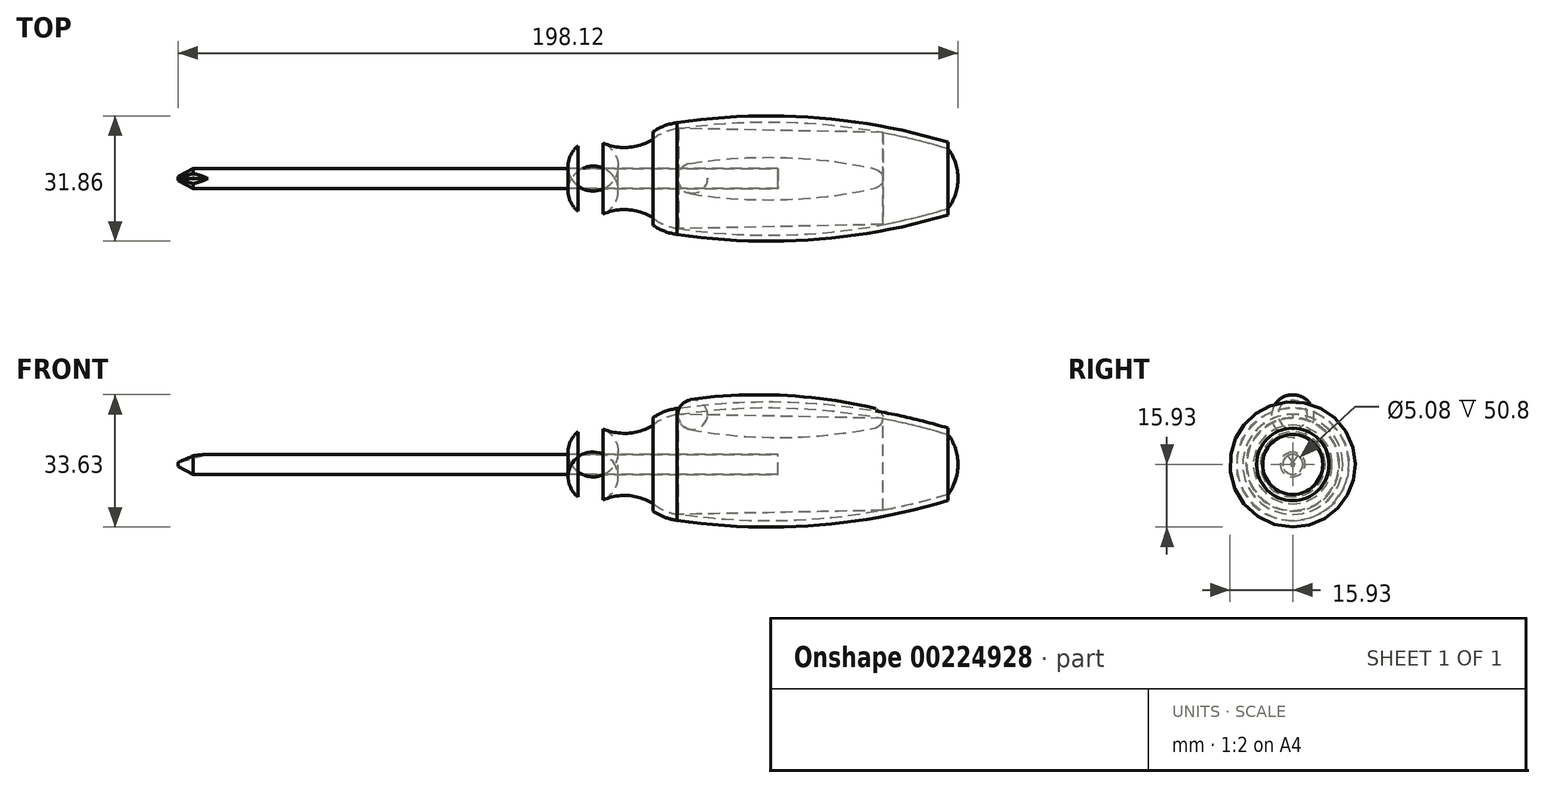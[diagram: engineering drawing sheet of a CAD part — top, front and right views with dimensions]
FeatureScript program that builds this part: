
annotation { "Feature Type Name" : "Feature", "Feature Type Description" : "" }
export const myFeature = defineFeature(function(context is Context, id is Id, definition is map)
    precondition{}
    {
        {
            var Q0;
            Q0=qCreatedBy(makeId("Front.planeOp"),FACE);
            var sketch = newSketch(context, id + "F0", { "sketchPlane" : qUnion([Q0])});
            skLineSegment(sketch, "E0", {"start": v(-101.6, 0) * mm, "end": v(0, 0) * mm});
            skLineSegment(sketch, "E1", {"start": v(0, 0) * mm, "end": v(96.52, 0) * mm});
            skLineSegment(sketch, "E2", {"start": v(0, 8.26) * mm, "end": v(0, 2.54) * mm});
            skLineSegment(sketch, "E3", {"start": v(0, 2.54) * mm, "end": v(-97.8, 2.54) * mm});
            skLineSegment(sketch, "E4", {"start": v(-97.8, 2.54) * mm, "end": v(-101.6, 0.5) * mm});
            skLineSegment(sketch, "E5", {"start": v(-101.6, 0.5) * mm, "end": v(-101.6, 0) * mm});
            skArc(sketch, "E6", {"start": v(6.35, 9.01) * mm, "mid": v(3.07, 9.5) * mm, "end": v(0, 8.26) * mm});
            skArc(sketch, "E7", {"start": v(6.35, 9.01) * mm, "mid": v(12.82, 7.93) * mm, "end": v(19.05, 10) * mm});
            skArc(sketch, "E8", {"start": v(25.4, 12.7) * mm, "mid": v(22.04, 11.78) * mm, "end": v(19.05, 10) * mm});
            skArc(sketch, "E9", {"start": v(96.52, 0) * mm, "mid": v(95.87, 4.02) * mm, "end": v(93.98, 7.62) * mm});
            skArc(sketch, "E10", {"start": v(93.98, 7.62) * mm, "mid": v(59.97, 13.98) * mm, "end": v(25.4, 12.7) * mm});
            skArc(sketch, "E11.0", {"start": v(25.2, 14.21) * mm, "mid": v(22, 13.4) * mm, "end": v(19.05, 11.88) * mm});
            skArc(sketch, "E12.0", {"start": v(93.98, 9.21) * mm, "mid": v(59.85, 15.52) * mm, "end": v(25.17, 14.2) * mm});
            skLineSegment(sketch, "E13", {"start": v(19.05, 10) * mm, "end": v(19.05, 11.88) * mm});
            skLineSegment(sketch, "E14", {"start": v(93.98, 9.21) * mm, "end": v(93.98, 7.62) * mm});
            skLineSegment(sketch, "E15", {"start": v(0, 2.54) * mm, "end": v(50.8, 2.54) * mm});
            skLineSegment(sketch, "E16", {"start": v(50.8, 2.54) * mm, "end": v(50.8, 0) * mm});
            skPoint(sketch, "E17", {"position": v(77.47, 11.69) * mm});
            skLineSegment(sketch, "E18", {"start": v(0, 0) * mm, "end": v(115.04, 0) * mm, "construction": true});
            skSolve(sketch);
        }
        {
            var Q0;
            Q0=makeQuery(id+"F0.imprint","IMPRINT",FACE,{"disambiguationData":[TD([[makeQuery(id+"F0.imprint","IMPRINT",EDGE,{"derivedFrom":sQuery(id+"F0.wireOp",EDGE,"E2")}),1.0]])]});
            var sketch = newSketch(context, id + "F1", { "sketchPlane" : qUnion([Q0])});
            skLineSegment(sketch, "E19", {"start": v(25.3, 12.73) * mm, "end": v(77.46, 11.69) * mm});
            skArc(sketch, "E20", {"start": v(28.6, 16.51) * mm, "mid": v(26.24, 15.24) * mm, "end": v(25.3, 12.73) * mm});
            skArc(sketch, "E21", {"start": v(77.46, 11.69) * mm, "mid": v(76.93, 13.28) * mm, "end": v(75.51, 14.2) * mm});
            skArc(sketch, "E22", {"start": v(75.51, 14.2) * mm, "mid": v(52.16, 17.54) * mm, "end": v(28.6, 16.51) * mm});
            skLineSegment(sketch, "E23", {"start": v(25.3, 12.73) * mm, "end": v(77.46, 11.69) * mm, "construction": true});
            skSolve(sketch);
        }
        {
            var Q0;
            {var subQ1=sQuery(id+"F0.wireOp",EDGE,"E0");Q0=makeQuery(id+"F0.imprint","IMPRINT",FACE,{"disambiguationData":[TD([[makeQuery(id+"F0.imprint","IMPRINT",EDGE,{"derivedFrom":subQ1}),1.0]])]});}
            var Q1;
            Q1=sQuery(id+"F0.wireOp",EDGE,"E18");
            revolve(context, id + "F2", {"entities" : qUnion([Q0]), "axis" : qUnion([Q1]), "revolveType" : RevolveType.FULL});
        }
        {
            var Q0;
            Q0=makeQuery(id+"F1.imprint","IMPRINT",FACE,{"disambiguationData":[TD([[makeQuery(id+"F1.imprint","IMPRINT",EDGE,{"derivedFrom":makeQuery(id+"F0.imprint","IMPRINT",EDGE,{"derivedFrom":sQuery(id+"F0.wireOp",EDGE,"E2")})}),1.0]])]});
            var Q1;
            Q1=makeQuery(id+"F2.opRevolve","SWEPT_FACE",FACE,{"disambiguationData":[OSD([sQuery(id+"F0.wireOp",EDGE,"E3"),sQuery(id+"F0.wireOp",EDGE,"E15")])]});
            revolve(context, id + "F3", {"entities" : qUnion([Q0]), "axis" : qUnion([Q1]), "revolveType" : RevolveType.FULL});
        }
        {
            var Q0;
            Q0=makeQuery(id+"F0.imprint","IMPRINT",FACE,{"disambiguationData":[TD([[makeQuery(id+"F0.imprint","IMPRINT",EDGE,{"derivedFrom":sQuery(id+"F0.wireOp",EDGE,"E8")}),-1.0]])]});
            var Q1;
            Q1=makeQuery(id+"F2.opRevolve","SWEPT_FACE",FACE,{"disambiguationData":[OSD([sQuery(id+"F0.wireOp",EDGE,"E3"),sQuery(id+"F0.wireOp",EDGE,"E15")])]});
            revolve(context, id + "F4", {"entities" : qUnion([Q0]), "axis" : qUnion([Q1]), "revolveType" : RevolveType.FULL});
        }
        {
            var Q0;
            Q0=qCreatedBy(makeId("Right.planeOp"),FACE);
            cPlane(context, id + "F5", {"entities" : qUnion([Q0]), "cplaneType" : CPlaneType.OFFSET, "offset" : 101.6 * mm, "oppositeDirection" : true, "width" : 152.4 * mm, "height" : 152.4 * mm});
        }
        {
            var Q0;
            Q0=qCreatedBy(id+"F5.planeOp",FACE);
            var sketch = newSketch(context, id + "F6", { "sketchPlane" : qUnion([Q0])});
            skLineSegment(sketch, "E24", {"start": v(0, 0.5) * mm, "end": v(0, 3.05) * mm});
            skLineSegment(sketch, "E25", {"start": v(0, 3.05) * mm, "end": v(5.08, 3.05) * mm});
            skLineSegment(sketch, "E26.MirrorCS", {"start": v(0, 3.05) * mm, "end": v(-5.08, 3.05) * mm});
            skLineSegment(sketch, "E27", {"start": v(5.08, 3.05) * mm, "end": v(0, 0.5) * mm});
            skLineSegment(sketch, "E28", {"start": v(-5.08, 3.05) * mm, "end": v(0, 0.5) * mm});
            skSolve(sketch);
        }
        {
            var Q0;
            Q0=qCreatedBy(makeId("Front.planeOp"),FACE);
            var sketch = newSketch(context, id + "F7", { "sketchPlane" : qUnion([Q0])});
            skLineSegment(sketch, "E29", {"start": v(-101.6, 0.5) * mm, "end": v(-93.98, 2.54) * mm});
            skSolve(sketch);
        }
        {
            var Q0;
            Q0 = qSketchRegion(id + "F6", true);
            var Q1;
            Q1 = qConstructionFilter(qBodyType(qCreatedBy(id + "F6" ,EDGE), BodyType.WIRE), ConstructionObject.NO);
            var Q2;
            Q2=sQuery(id+"F7.wireOp",EDGE,"E29");
            sweep(context, id + "F8", {"operationType" : NewBodyOperationType.REMOVE, "profiles" : qUnion([Q0]), "surfaceProfiles" : qUnion([Q1]), "path" : qUnion([Q2])});
        }
        {
            var Q0;
            {var subQ6=sQuery(id+"F1.wireOp",EDGE,"E20");Q0=makeQuery(id+"F1.imprint","IMPRINT",FACE,{"disambiguationData":[TD([[makeQuery(id+"F1.imprint","IMPRINT",EDGE,{"derivedFrom":subQ6}),1.0]])]});}
            var Q1;
            {var subQ0=sQuery(id+"F1.wireOp",EDGE,"E21");var subQ1=sQuery(id+"F1.wireOp",EDGE,"E19");var subQ2=makeQuery(id+"F1.imprint","INTERSECT",VERTEX,{"derivedFrom":[subQ1,subQ0]});Q1=makeQuery(id+"F1.imprint","IMPRINT",FACE,{"disambiguationData":[TD([[makeQuery(id+"F1.imprint","IMPRINT",EDGE,{"disambiguationData":[TD([[subQ2,1.0]])],"derivedFrom":subQ1}),1.0]])]});}
            var Q2;
            Q2=sQuery(id+"F1.wireOp",EDGE,"E19");
            revolve(context, id + "F9", {"entities" : qUnion([Q0, Q1]), "axis" : qUnion([Q2]), "revolveType" : RevolveType.FULL});
        }
        {
            var Q0;
            Q0=makeQuery(id+"F3.opRevolve","SWEPT_BODY",BODY,{"disambiguationData":[OSD([sQuery(id+"F0.wireOp",EDGE,"E1"),sQuery(id+"F0.wireOp",EDGE,"E2"),sQuery(id+"F0.wireOp",EDGE,"E6"),sQuery(id+"F0.wireOp",EDGE,"E7"),sQuery(id+"F0.wireOp",EDGE,"E8"),sQuery(id+"F0.wireOp",EDGE,"E9"),sQuery(id+"F0.wireOp",EDGE,"E10"),sQuery(id+"F0.wireOp",EDGE,"E15"),sQuery(id+"F0.wireOp",EDGE,"E16"),sQuery(id+"F1.wireOp",EDGE,"E19"),sQuery(id+"F1.wireOp",EDGE,"E21")])]});
            var Q1;
            Q1=makeQuery(id+"F4.opRevolve","SWEPT_BODY",BODY,{"disambiguationData":[OSD([sQuery(id+"F0.wireOp",EDGE,"E8"),sQuery(id+"F0.wireOp",EDGE,"E10"),sQuery(id+"F0.wireOp",EDGE,"E11.0"),sQuery(id+"F0.wireOp",EDGE,"E12.0"),sQuery(id+"F0.wireOp",EDGE,"E13"),sQuery(id+"F0.wireOp",EDGE,"E14")])]});
            booleanBodies(context, id + "F10", {"operationType" : BooleanOperationType.SUBTRACTION, "tools" : qUnion([Q0]), "targets" : qUnion([Q1]), "keepTools" : true});
        }
    });
